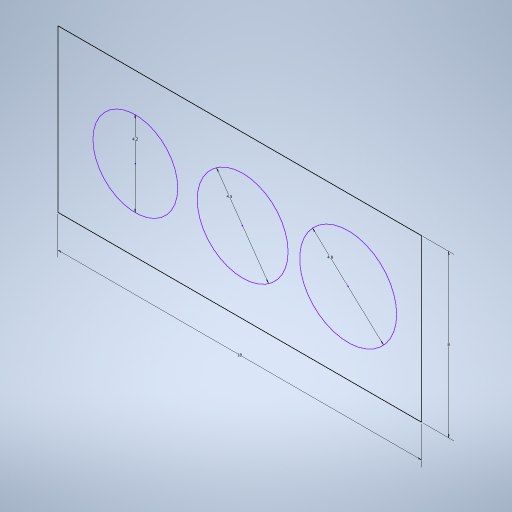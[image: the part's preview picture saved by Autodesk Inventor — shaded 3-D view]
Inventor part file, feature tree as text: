
AUTODESK INVENTOR PART (.ipt)
format: ipt  version: 2023 (Build 270158000, 158)  size: 243,200 bytes
history: native  units: in
note: dims shown in document units (in); Inventor stores cm internally (conversion verified against a paired STEP export)
features: sketch x1
ambient origin geometry x8: Origin, YZ Plane, XZ Plane, XY Plane, X Axis, Y Axis, Z Axis, Center Point
feature tree (1):
  sketch  "Sketch6"  dims[d11=0.7087in d12=0.315in d13=0.1654in d14=0.1772in d15=0.189in]
